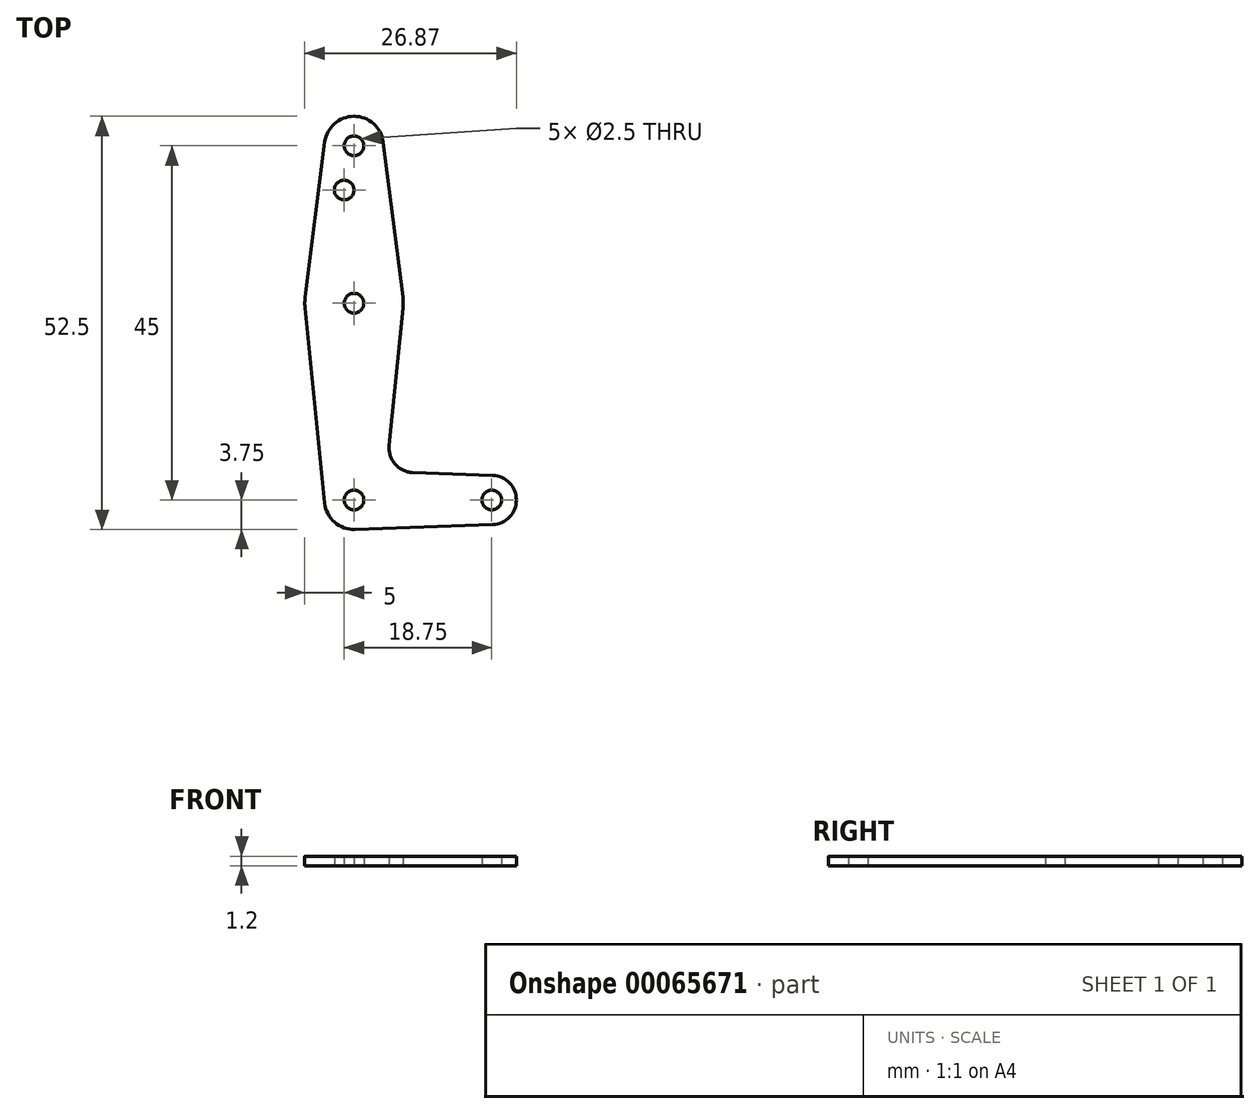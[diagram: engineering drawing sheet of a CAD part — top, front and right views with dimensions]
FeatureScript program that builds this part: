
annotation { "Feature Type Name" : "Feature", "Feature Type Description" : "" }
export const myFeature = defineFeature(function(context is Context, id is Id, definition is map)
    precondition{}
    {
        {
            var Q0;
            Q0=qCreatedBy(makeId("Top.planeOp"),FACE);
            var sketch = newSketch(context, id + "F0", { "sketchPlane" : qUnion([Q0])});
            skLineSegment(sketch, "E0", {"start": v(0, 0) * mm, "end": v(17.5, 0) * mm, "construction": true});
            skLineSegment(sketch, "E1", {"start": v(0, 0) * mm, "end": v(0, 45) * mm, "construction": true});
            skCircle(sketch, "E2", {"center": v(0, 45) * mm, "radius": 3.75 * mm});
            skCircle(sketch, "E3", {"center": v(0, 25) * mm, "radius": 6.25 * mm});
            skCircle(sketch, "E4", {"center": v(0, 0) * mm, "radius": 3.75 * mm});
            skCircle(sketch, "E5", {"center": v(17.5, 0) * mm, "radius": 3.12 * mm});
            skLineSegment(sketch, "E6", {"start": v(3.72, 45.47) * mm, "end": v(6.2, 25.78) * mm});
            skLineSegment(sketch, "E7", {"start": v(-6.2, 25.78) * mm, "end": v(-3.72, 45.47) * mm});
            skLineSegment(sketch, "E8", {"start": v(6.22, 24.38) * mm, "end": v(4.47, 6.93) * mm});
            skLineSegment(sketch, "E9", {"start": v(-3.73, -0.38) * mm, "end": v(-6.22, 24.38) * mm});
            skLineSegment(sketch, "E10", {"start": v(7.47, 3.49) * mm, "end": v(17.61, 3.12) * mm});
            skLineSegment(sketch, "E11", {"start": v(0.13, -3.75) * mm, "end": v(17.61, -3.12) * mm});
            skCircle(sketch, "E12", {"center": v(0, 45) * mm, "radius": 1.25 * mm});
            skCircle(sketch, "E13", {"center": v(-1.25, 39.38) * mm, "radius": 1.25 * mm});
            skCircle(sketch, "E14", {"center": v(0, 25) * mm, "radius": 1.25 * mm});
            skCircle(sketch, "E15", {"center": v(0, 0) * mm, "radius": 1.25 * mm});
            skCircle(sketch, "E16", {"center": v(17.5, 0) * mm, "radius": 1.25 * mm});
            skArc(sketch, "E17.filletArc", {"start": v(4.47, 6.93) * mm, "mid": v(5.22, 4.56) * mm, "end": v(7.47, 3.49) * mm});
            skSolve(sketch);
        }
        {
            var Q0;
            Q0 = qSketchRegion(id + "F0", true);
            extrude(context, id + "F1", {"entities" : qUnion([Q0]), "depth" : 1.2 * mm});
        }
    });
